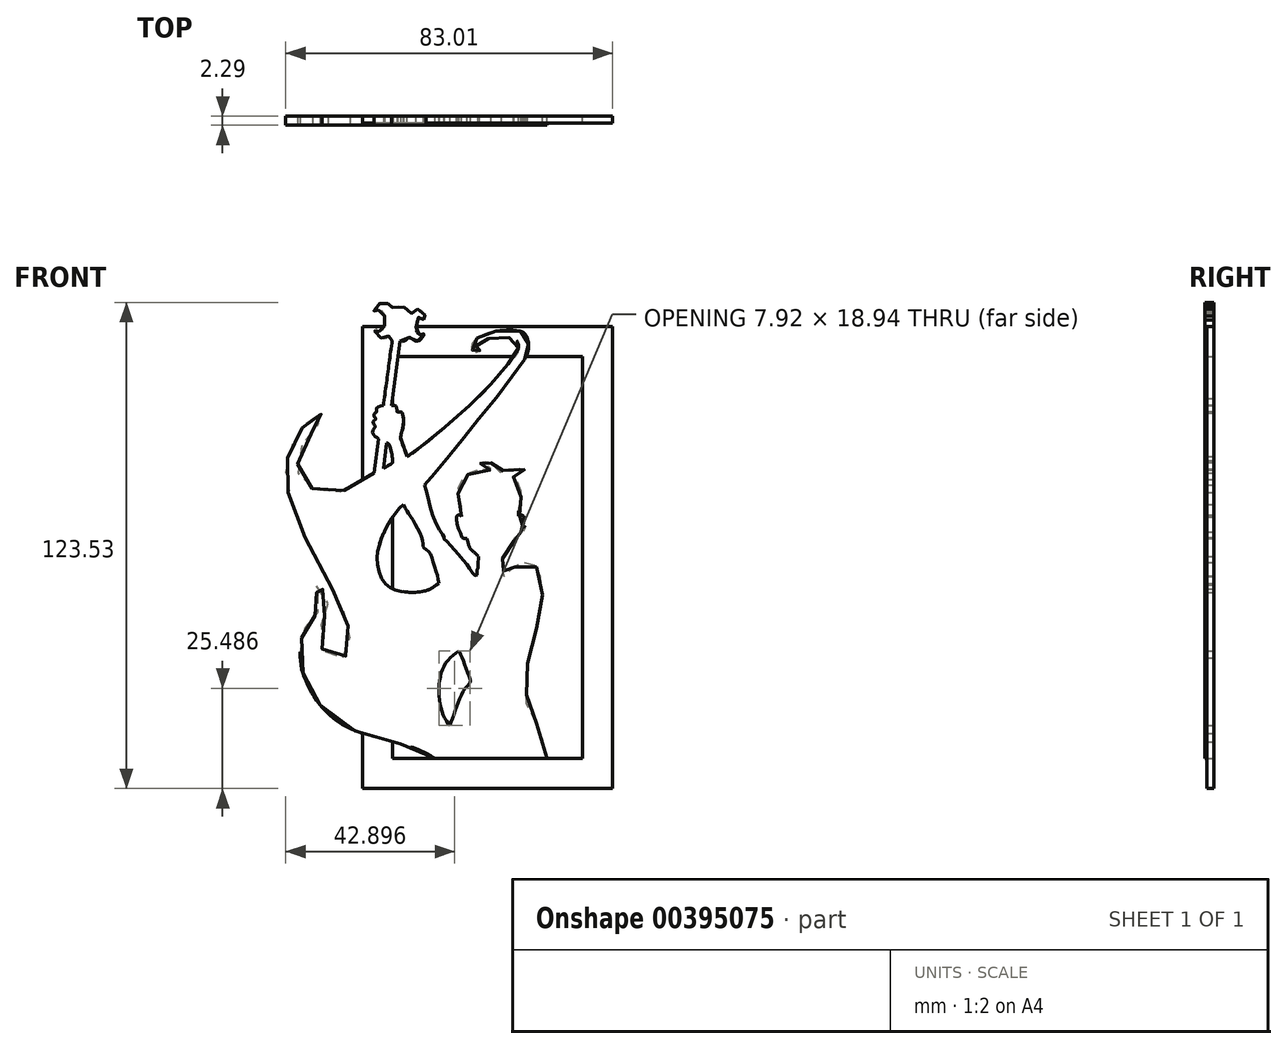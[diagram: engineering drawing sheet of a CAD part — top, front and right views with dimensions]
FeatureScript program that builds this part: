
annotation { "Feature Type Name" : "Feature", "Feature Type Description" : "" }
export const myFeature = defineFeature(function(context is Context, id is Id, definition is map)
    precondition{}
    {
        {
            var Q0;
            Q0=qCreatedBy(makeId("Front.planeOp"),FACE);
            var sketch = newSketch(context, id + "F0", { "sketchPlane" : qUnion([Q0])});
            skLineSegment(sketch, "E0.bottom", {"start": v(31.75, 58.67) * mm, "end": v(-31.75, 58.67) * mm});
            skLineSegment(sketch, "E0.top", {"start": v(31.75, -58.67) * mm, "end": v(-31.75, -58.67) * mm});
            skLineSegment(sketch, "E0.left", {"start": v(31.75, 58.67) * mm, "end": v(31.75, -58.67) * mm});
            skLineSegment(sketch, "E0.right", {"start": v(-31.75, 58.67) * mm, "end": v(-31.75, -58.67) * mm});
            skPoint(sketch, "E0.middle", {"position": v(0, 0) * mm});
            skLineSegment(sketch, "E1.0", {"start": v(-24.13, 51.05) * mm, "end": v(-24.13, -51.05) * mm});
            skLineSegment(sketch, "E1.1", {"start": v(24.13, 51.05) * mm, "end": v(-24.13, 51.05) * mm});
            skLineSegment(sketch, "E1.2", {"start": v(24.13, 51.05) * mm, "end": v(24.13, -51.05) * mm});
            skLineSegment(sketch, "E1.3", {"start": v(24.13, -51.05) * mm, "end": v(-24.13, -51.05) * mm});
            skSolve(sketch);
        }
        {
            var Q0;
            Q0=qSketchRegion(id+"F0",true);
            extrude(context, id + "F1", {"entities" : qUnion([Q0]), "depth" : 1.78 * mm});
        }
        {
            var Q0;
            Q0=qCreatedBy(makeId("Front.planeOp"),FACE);
            var sketch = newSketch(context, id + "F2", { "sketchPlane" : qUnion([Q0])});
            skLineSegment(sketch, "E2", {"start": v(-13.4, -51.05) * mm, "end": v(15.1, -51.05) * mm});
            skFitSpline(sketch, "E3", {"points": [v(15.1, -51.05) * mm, v(14.07, -46.67) * mm, v(12.43, -42.04) * mm, v(9.81, -36.93) * mm, v(9.63, -36.63) * mm, v(9.93, -34.8) * mm, v(10.11, -30.42) * mm, v(10, -28.05) * mm, v(10.78, -23.49) * mm, v(11.88, -19.96) * mm, v(13.1, -14.91) * mm, v(13.7, -11.8) * mm, v(13.89, -7.61) * mm, v(13.4, -4.75) * mm, v(12.55, -2.56) * mm, v(11.09, -1.47) * mm, v(9.26, -1.22) * mm, v(7.38, -2.07) * mm, v(5.8, -3.17) * mm, v(4.21, -4.81) * mm, v(4.14, -4.64) * mm, v(4.07, -4) * mm, v(3.98, -2.7) * mm, v(3.9, -1.79) * mm, v(3.64, -1.38) * mm, v(3.56, -0.75) * mm, v(3.58, -0.38) * mm, v(3.68, -0.29) * mm, v(4.73, 1.03) * mm, v(6.12, 2.95) * mm, v(6.51, 3.62) * mm, v(6.68, 4.16) * mm, v(6.81, 5.02) * mm, v(6.96, 5.1) * mm, v(7.28, 5.02) * mm, v(7.6, 5.21) * mm, v(8.02, 6) * mm, v(8.47, 6.55) * mm, v(8.64, 6.5) * mm, v(9, 6.57) * mm, v(9.37, 6.93) * mm, v(9.65, 7.2) * mm, v(9.74, 7.51) * mm, v(9.41, 7.86) * mm, v(8.96, 8.12) * mm, v(8.88, 8.22) * mm, v(9.1, 8.8) * mm, v(9.33, 9.94) * mm, v(9.1, 10.6) * mm, v(8.6, 10.87) * mm, v(8.06, 10.68) * mm, v(7.9, 10.61) * mm, v(7.82, 11.24) * mm, v(8.08, 13.09) * mm, v(8.49, 15.24) * mm, v(8.51, 17.21) * mm, v(7.93, 18.74) * mm, v(6.68, 20.42) * mm, v(6.57, 20.6) * mm, v(6.81, 21) * mm, v(7.84, 21.69) * mm, v(9.05, 21.99) * mm, v(9.28, 22.03) * mm, v(9.4, 22.3) * mm, v(9.18, 22.48) * mm, v(8.1, 22.57) * mm, v(6.34, 22.5) * mm, v(4.1, 22.18) * mm, v(3.11, 21.54) * mm, v(2.94, 21.52) * mm, v(2.75, 22.05) * mm, v(1.82, 23.2) * mm, v(0.72, 24.18) * mm, v(0.27, 24.27) * mm, v(-0.57, 24.36) * mm, v(-1.88, 24.33) * mm, v(-2, 24.14) * mm, v(-2.1, 24.03) * mm, v(-1.43, 23.93) * mm, v(-0.7, 23.84) * mm, v(0.06, 23.45) * mm, v(0.88, 22.55) * mm, v(0.94, 22.38) * mm, v(0.77, 22.3) * mm, v(-0.07, 22.38) * mm, v(-1.68, 22.5) * mm, v(-3.92, 21.84) * mm, v(-5.66, 20.66) * mm, v(-7, 19.1) * mm, v(-7.5, 17.62) * mm, v(-7.45, 15.99) * mm, v(-6.95, 14.07) * mm, v(-6.76, 12.57) * mm, v(-6.67, 10.48) * mm], "startDerivative": vector(-46.05, 210) * mm, "endDerivative": vector(5, -150.86) * mm});
            skFitSpline(sketch, "E4", {"points": [v(-6.67, 10.48) * mm, v(-6.98, 10.76) * mm, v(-7.56, 10.76) * mm, v(-7.86, 10.48) * mm, v(-7.86, 9.69) * mm, v(-7.75, 8.53) * mm, v(-7.36, 7.36) * mm, v(-6.67, 5.86) * mm, v(-6.4, 5.04) * mm, v(-6, 4.91) * mm, v(-5.5, 4.91) * mm, v(-5.23, 4.91) * mm], "startDerivative": vector(-3.53, 4.78) * mm, "endDerivative": vector(4.22, -0.04) * mm});
            skFitSpline(sketch, "E5", {"points": [v(-5.23, 4.91) * mm, v(-4.96, 3.81) * mm, v(-4.57, 2.56) * mm, v(-4.18, 2.09) * mm, v(-3, 1.01) * mm, v(-2.35, 0.35) * mm], "startDerivative": vector(1.27, -5.08) * mm, "endDerivative": vector(3, -3.27) * mm});
            skFitSpline(sketch, "E6", {"points": [v(-2.35, 0.35) * mm, v(-2.35, -2.34) * mm, v(-2.35, -2.62) * mm, v(-2.54, -2.68) * mm, v(-2.64, -2.87) * mm, v(-2.7, -3.57) * mm, v(-2.77, -4.6) * mm, v(-2.85, -4.6) * mm, v(-3.2, -4.52) * mm, v(-3.68, -4.07) * mm, v(-4.42, -3.05) * mm, v(-5.06, -1.92) * mm, v(-6.18, -0.65) * mm, v(-7.56, 1.04) * mm, v(-8.8, 2.46) * mm, v(-9.78, 3.55) * mm, v(-10.71, 4.44) * mm, v(-11.04, 4.73) * mm, v(-11.01, 4.82) * mm, v(-10.99, 5.13) * mm, v(-11.07, 5.59) * mm, v(-11.36, 5.9) * mm, v(-12.1, 6.94) * mm, v(-13.57, 9.83) * mm, v(-14.78, 13.68) * mm, v(-15.57, 17) * mm, v(-16.05, 18.49) * mm], "startDerivative": vector(-1.4, -53.24) * mm, "endDerivative": vector(-9.98, 28.07) * mm});
            skFitSpline(sketch, "E7", {"points": [v(-16.05, 18.49) * mm, v(-14.44, 20.22) * mm, v(-11.08, 24.27) * mm, v(-6.56, 29.7) * mm, v(-2.54, 34.9) * mm, v(3.63, 42.43) * mm, v(7.76, 48.1) * mm, v(10.1, 51.74) * mm, v(10.35, 54.81) * mm, v(9.05, 57.24) * mm, v(2.42, 57.56) * mm, v(-2.54, 55.86) * mm, v(-4.06, 53.76) * mm, v(-3.49, 52.3) * mm, v(-2.54, 52.3) * mm, v(-1.98, 52.6) * mm, v(-2.35, 52.97) * mm, v(-2.96, 53.2) * mm, v(-2.93, 53.79) * mm, v(-1.4, 55.05) * mm, v(2.82, 56) * mm, v(7.18, 55.28) * mm, v(7.75, 52.97) * mm, v(5.03, 48.99) * mm, v(-1.09, 42.07) * mm, v(-9.94, 33.99) * mm, v(-18.22, 27.16) * mm, v(-20.43, 25.76) * mm], "startDerivative": vector(51.48, 53.06) * mm, "endDerivative": vector(-61.57, -34.52) * mm});
            skFitSpline(sketch, "E8", {"points": [v(-21.38, 13.54) * mm, v(-23.4, 11.35) * mm, v(-25.9, 7.27) * mm, v(-27.77, 2.2) * mm, v(-27.9, -1.84) * mm, v(-26.2, -6.4) * mm, v(-23.52, -8.1) * mm, v(-19.48, -8.8) * mm, v(-14.86, -8.1) * mm, v(-13.2, -7.06) * mm, v(-12.32, -6.57) * mm], "startDerivative": vector(-21.98, -21.6) * mm, "endDerivative": vector(16.25, 7.7) * mm});
            skFitSpline(sketch, "E9", {"points": [v(-12.32, -6.57) * mm, v(-12.92, -3.86) * mm, v(-14.01, -0.42) * mm, v(-14.9, 1.56) * mm, v(-16.05, 2.41) * mm, v(-16.4, 2.94) * mm, v(-16.44, 4.15) * mm, v(-17.5, 6.94) * mm, v(-19.27, 10.14) * mm, v(-20.37, 11.68) * mm, v(-21.38, 13.54) * mm], "startDerivative": vector(-4.4, 22.74) * mm, "endDerivative": vector(-9.9, 19.78) * mm});
            skFitSpline(sketch, "E10", {"points": [v(-20.43, 25.76) * mm, v(-22.05, 30.3) * mm, v(-22.05, 30.93) * mm, v(-21.38, 34.16) * mm, v(-21.62, 36.65) * mm, v(-21.83, 36.92) * mm, v(-22.26, 36.96) * mm, v(-22.9, 36.98) * mm, v(-23.02, 37.14) * mm, v(-23.02, 37.92) * mm, v(-23.43, 38.6) * mm, v(-23.82, 38.67) * mm, v(-24.35, 38.64) * mm], "startDerivative": vector(-11.78, 31.34) * mm, "endDerivative": vector(-9.1, -0.56) * mm});
            skFitSpline(sketch, "E11", {"points": [v(-24.35, 38.64) * mm, v(-22.2, 55) * mm], "startDerivative": vector(2.14, 16.36) * mm, "endDerivative": vector(2.14, 16.36) * mm});
            skFitSpline(sketch, "E12", {"points": [v(-26.49, 38.64) * mm, v(-24.21, 55.2) * mm], "startDerivative": vector(2.38, 16.57) * mm, "endDerivative": vector(2.38, 16.57) * mm});
            skFitSpline(sketch, "E13", {"points": [v(-27.68, 30.19) * mm, v(-28.84, 21.57) * mm], "startDerivative": vector(-1.15, -8.61) * mm, "endDerivative": vector(-1.15, -8.61) * mm});
            skFitSpline(sketch, "E14", {"points": [v(-25.71, 29.13) * mm, v(-26.43, 22.68) * mm], "startDerivative": vector(-0.72, -6.45) * mm, "endDerivative": vector(-0.72, -6.45) * mm});
            skFitSpline(sketch, "E15", {"points": [v(-22.2, 55) * mm, v(-20.81, 55.2) * mm, v(-19.8, 56) * mm, v(-18.75, 55.2) * mm, v(-17.3, 55.2) * mm, v(-16.28, 56.5) * mm, v(-16.2, 56.74) * mm, v(-16.26, 56.92) * mm, v(-16.75, 56.72) * mm, v(-17.25, 56.72) * mm, v(-17.9, 57.3) * mm, v(-18.22, 58.17) * mm, v(-18.08, 59.68) * mm, v(-17.68, 60.96) * mm, v(-17.03, 61.38) * mm, v(-16.52, 60.93) * mm, v(-16.2, 60.47) * mm, v(-15.78, 60.51) * mm, v(-15.66, 60.97) * mm, v(-16.36, 62.31) * mm, v(-17.45, 63.13) * mm, v(-18.36, 62.87) * mm, v(-19.08, 62.04) * mm, v(-19.24, 62.09) * mm, v(-20, 62.93) * mm, v(-21.57, 63.82) * mm, v(-23.57, 63.77) * mm, v(-24.35, 63.4) * mm, v(-24.35, 63.56) * mm, v(-25.19, 64.43) * mm, v(-25.97, 64.83) * mm, v(-27.22, 64.66) * mm, v(-28.48, 63.6) * mm, v(-28.88, 62.83) * mm, v(-28.7, 62.46) * mm, v(-28.42, 62.43) * mm, v(-27.88, 62.73) * mm, v(-27.43, 62.97) * mm, v(-26.36, 62.07) * mm, v(-26.07, 60.63) * mm, v(-26.15, 59.08) * mm, v(-26.68, 57.98) * mm, v(-27.32, 57.5) * mm, v(-27.93, 57.64) * mm, v(-28.22, 58.04) * mm, v(-28.66, 57.78) * mm, v(-28.3, 56.98) * mm, v(-27.36, 56) * mm, v(-25.95, 55.8) * mm, v(-25.22, 56.23) * mm, v(-25.02, 56.23) * mm, v(-24.69, 55.76) * mm, v(-24.35, 55.38) * mm, v(-24.21, 55.2) * mm], "startDerivative": vector(61, -3.49) * mm, "endDerivative": vector(21.54, -13.38) * mm});
            skFitSpline(sketch, "E16", {"points": [v(-26.43, 22.68) * mm, v(-25, 23.53) * mm, v(-24.35, 23.94) * mm, v(-24.06, 24.26) * mm, v(-24.08, 24.4) * mm, v(-24.21, 25.67) * mm, v(-24.63, 27.78) * mm, v(-25.16, 28.98) * mm, v(-25.71, 29.13) * mm], "startDerivative": vector(10.83, 5.27) * mm, "endDerivative": vector(-6.22, 0.36) * mm});
            skFitSpline(sketch, "E17", {"points": [v(-28.84, 21.57) * mm, v(-34.02, 18.49) * mm, v(-38.02, 16.6) * mm, v(-43.02, 16.99) * mm, v(-46.92, 19.2) * mm, v(-48.26, 23.2) * mm, v(-46.77, 29.13) * mm, v(-43.16, 33.88) * mm, v(-42.3, 34.74) * mm, v(-42.06, 35.95) * mm, v(-42.4, 36.52) * mm, v(-43.84, 36.19) * mm, v(-46.53, 33.64) * mm, v(-48.9, 30.32) * mm, v(-50.91, 24.83) * mm, v(-51.15, 19.54) * mm, v(-49.47, 12.88) * mm, v(-43.93, 0.35) * mm, v(-37.37, -11.93) * mm, v(-35.51, -17.27) * mm, v(-34.98, -22.19) * mm, v(-36.4, -25.25) * mm, v(-40.08, -25.25) * mm, v(-42.2, -22.73) * mm, v(-42.12, -16.88) * mm, v(-40.83, -13.34) * mm, v(-40.7, -10) * mm, v(-43.23, -7.13) * mm, v(-44.38, -7.42) * mm, v(-44.33, -8.1) * mm, v(-42.94, -9.2) * mm, v(-42.27, -11.9) * mm, v(-44.14, -15.02) * mm, v(-46.26, -17.52) * mm, v(-47.32, -20.55) * mm, v(-47.56, -26.18) * mm, v(-46.07, -31.57) * mm, v(-42.8, -37.1) * mm, v(-36.68, -42.54) * mm, v(-26.97, -46.05) * mm, v(-18.22, -48.5) * mm, v(-13.4, -51.05) * mm], "startDerivative": vector(-190.43, -112.05) * mm, "endDerivative": vector(158.52, -121.25) * mm});
            skFitSpline(sketch, "E18", {"points": [v(-7.22, -23.71) * mm, v(-5.68, -27.43) * mm, v(-4.42, -31.1) * mm, v(-4.48, -31.78) * mm, v(-5.96, -33.61) * mm, v(-8.02, -38.3) * mm, v(-9.57, -42.65) * mm], "startDerivative": vector(8.08, -18.75) * mm, "endDerivative": vector(-7.48, -20.99) * mm});
            skFitSpline(sketch, "E19", {"points": [v(-7.22, -23.71) * mm, v(-10.43, -26.46) * mm, v(-12.03, -30.47) * mm, v(-12.31, -35.16) * mm, v(-11.23, -40.02) * mm, v(-9.57, -42.65) * mm], "startDerivative": vector(-17.85, -12.27) * mm, "endDerivative": vector(10.47, -13.68) * mm});
            skFitSpline(sketch, "E20", {"points": [v(-26.49, 38.64) * mm, v(-27.78, 38.33) * mm, v(-28.2, 37.99) * mm, v(-28.16, 37.44) * mm, v(-28.2, 37.04) * mm, v(-28.35, 36.82) * mm, v(-28.71, 36.65) * mm, v(-28.9, 36) * mm, v(-28.43, 35.44) * mm, v(-28.52, 35.08) * mm, v(-29.1, 34.7) * mm, v(-28.9, 33.93) * mm, v(-28.54, 33.35) * mm, v(-28.71, 32.96) * mm, v(-29.16, 32.37) * mm, v(-29.12, 31.44) * mm, v(-28.28, 30.65) * mm, v(-27.68, 30.19) * mm], "startDerivative": vector(-16.9, -3.26) * mm, "endDerivative": vector(8.6, -6.94) * mm});
            skSolve(sketch);
        }
        {
            var Q0;
            Q0 = qSketchRegion(id + "F2", true);
            extrude(context, id + "F3", {"entities" : qUnion([Q0]), "operationType" : NewBodyOperationType.ADD, "depth" : 2.3 * mm});
        }
        {
            var Q0;
            Q0=makeQuery(id+"F3.opExtrude","CAP_FACE",FACE,{"disambiguationData":[OSD([sQuery(id+"F2.wireOp",EDGE,"E2"),sQuery(id+"F2.wireOp",EDGE,"E3"),sQuery(id+"F2.wireOp",EDGE,"E4"),sQuery(id+"F2.wireOp",EDGE,"E5"),sQuery(id+"F2.wireOp",EDGE,"E6"),sQuery(id+"F2.wireOp",EDGE,"E7"),sQuery(id+"F2.wireOp",EDGE,"E8"),sQuery(id+"F2.wireOp",EDGE,"E9"),sQuery(id+"F2.wireOp",EDGE,"E10"),sQuery(id+"F2.wireOp",EDGE,"E11"),sQuery(id+"F2.wireOp",EDGE,"E12"),sQuery(id+"F2.wireOp",EDGE,"E13"),sQuery(id+"F2.wireOp",EDGE,"E14"),sQuery(id+"F2.wireOp",EDGE,"E15"),sQuery(id+"F2.wireOp",EDGE,"E16"),sQuery(id+"F2.wireOp",EDGE,"E17"),sQuery(id+"F2.wireOp",EDGE,"E18"),sQuery(id+"F2.wireOp",EDGE,"E19"),sQuery(id+"F2.wireOp",EDGE,"E20")])],"isStart":false});
            var sketch = newSketch(context, id + "F4", { "sketchPlane" : qUnion([Q0])});
            skFitSpline(sketch, "E21", {"points": [v(-7.2, 9.05) * mm, v(-6.76, 8.3) * mm, v(-6.3, 7.67) * mm], "startDerivative": vector(0.82, -1.5) * mm, "endDerivative": vector(1, -1.24) * mm});
            skFitSpline(sketch, "E22", {"points": [v(-5.54, 6.57) * mm, v(-5.39, 5.64) * mm, v(-5.31, 5.12) * mm], "startDerivative": vector(0.3, -1.75) * mm, "endDerivative": vector(0.16, -1.12) * mm});
            skFitSpline(sketch, "E23", {"points": [v(-6.57, 10.34) * mm, v(-6.14, 9.6) * mm, v(-5.56, 8.59) * mm, v(-5.54, 8.75) * mm, v(-5.54, 11) * mm, v(-5.64, 12.95) * mm, v(-4.93, 15.58) * mm, v(-4.48, 16.16) * mm, v(-4.34, 16.17) * mm, v(-4.18, 15.4) * mm, v(-3.71, 13.67) * mm, v(-2.7, 12.31) * mm, v(-2.26, 11.98) * mm, v(-2.12, 12.33) * mm, v(-1.94, 13.7) * mm, v(-0.41, 16.17) * mm, v(0.35, 16.83) * mm, v(0.53, 16.83) * mm, v(1.18, 16.38) * mm, v(2.03, 15.52) * mm, v(3.01, 13.36) * mm, v(3.4, 12.3) * mm, v(3.6, 12.14) * mm, v(3.86, 12.1) * mm, v(4.72, 13.44) * mm, v(5.55, 15.16) * mm, v(5.94, 15.36) * mm, v(6.17, 15.06) * mm, v(6.47, 13.64) * mm, v(6.76, 10.98) * mm, v(6.74, 8.65) * mm, v(6.84, 8.29) * mm, v(7.05, 8.2) * mm, v(7.24, 9.05) * mm, v(7.84, 10.5) * mm], "startDerivative": vector(14.17, -22.21) * mm, "endDerivative": vector(20.52, 38.76) * mm});
            skFitSpline(sketch, "E24", {"points": [v(7.05, 7.94) * mm, v(7.02, 7.04) * mm, v(6.85, 5.88) * mm, v(6.9, 5.35) * mm], "startDerivative": vector(0.04, -2.48) * mm, "endDerivative": vector(0.33, -1.79) * mm});
            skFitSpline(sketch, "E25", {"points": [v(8.87, 8.02) * mm, v(8.45, 8) * mm, v(8.5, 7.5) * mm, v(8.98, 7.24) * mm, v(9.32, 7.07) * mm], "startDerivative": vector(-2.15, 0.38) * mm, "endDerivative": vector(1.37, -0.8) * mm});
            skFitSpline(sketch, "E26", {"points": [v(8.5, 7.32) * mm, v(8.48, 7.02) * mm, v(8.52, 6.74) * mm], "startDerivative": vector(-0.1, -0.6) * mm, "endDerivative": vector(0.13, -0.57) * mm});
            skFitSpline(sketch, "E27", {"points": [v(-6.67, 15.66) * mm, v(-6.32, 17.88) * mm, v(-4.47, 19.57) * mm, v(-2.44, 19.94) * mm], "startDerivative": vector(0.06, 6.93) * mm, "endDerivative": vector(6.4, 0.37) * mm});
            skFitSpline(sketch, "E28", {"points": [v(-4.28, 19.97) * mm, v(-3.31, 20.91) * mm, v(-0.94, 21.48) * mm, v(0.81, 21.38) * mm, v(1.35, 20.88) * mm], "startDerivative": vector(3.31, 4.38) * mm, "endDerivative": vector(2.42, -3.33) * mm});
            skFitSpline(sketch, "E29", {"points": [v(2.93, 21.03) * mm, v(3.66, 21.22) * mm, v(4.12, 21.74) * mm], "startDerivative": vector(1.56, 0.19) * mm, "endDerivative": vector(0.8, 1.23) * mm});
            skFitSpline(sketch, "E30", {"points": [v(-2.88, 9.75) * mm, v(-2.83, 9.25) * mm, v(-2.35, 8.83) * mm, v(-2.03, 8.87) * mm, v(-1.73, 9.4) * mm, v(-1.69, 9.63) * mm], "startDerivative": vector(-0.2, -2.4) * mm, "endDerivative": vector(0.08, 1.38) * mm});
            skFitSpline(sketch, "E31", {"points": [v(-3.76, 8.94) * mm, v(-4.1, 9.58) * mm, v(-3.6, 10.2) * mm, v(-2.73, 10) * mm, v(-1.6, 9.85) * mm, v(-0.42, 9.54) * mm], "startDerivative": vector(-2.96, 3.38) * mm, "endDerivative": vector(5.18, -1.68) * mm});
            skFitSpline(sketch, "E32", {"points": [v(0.04, 9.9) * mm, v(-1.06, 10.18) * mm, v(-2.35, 10.8) * mm, v(-3.67, 11.55) * mm], "startDerivative": vector(-3.54, 0.76) * mm, "endDerivative": vector(-3.71, 2.15) * mm});
            skFitSpline(sketch, "E33", {"points": [v(2.7, 9.67) * mm, v(3.48, 10.08) * mm, v(5.05, 10.2) * mm, v(5.7, 10) * mm, v(5.65, 9.68) * mm, v(5.07, 8.93) * mm], "startDerivative": vector(3.3, 2.27) * mm, "endDerivative": vector(-3.22, -3.72) * mm});
            skFitSpline(sketch, "E34", {"points": [v(3.32, 9.8) * mm, v(3.53, 9.23) * mm, v(3.88, 8.97) * mm, v(4.28, 9.05) * mm, v(4.48, 9.43) * mm, v(4.48, 10.04) * mm], "startDerivative": vector(0.75, -2.77) * mm, "endDerivative": vector(-0.21, 2.84) * mm});
            skFitSpline(sketch, "E35", {"points": [v(2.53, 10.14) * mm, v(3.44, 10.7) * mm, v(4.44, 11.11) * mm, v(5.7, 11.5) * mm], "startDerivative": vector(2.8, 1.82) * mm, "endDerivative": vector(3.61, 1.08) * mm});
            skFitSpline(sketch, "E36", {"points": [v(0.68, 5.35) * mm, v(0.51, 5.26) * mm, v(0.52, 5.03) * mm, v(0.8, 4.91) * mm, v(0.87, 5.19) * mm, v(0.68, 5.35) * mm]});
            skFitSpline(sketch, "E37", {"points": [v(1.76, 5.07) * mm, v(2.03, 5.35) * mm, v(2.3, 5.35) * mm, v(2.46, 5.2) * mm, v(2.28, 4.82) * mm, v(2.03, 4.7) * mm, v(1.8, 4.82) * mm, v(1.76, 5.07) * mm]});
            skFitSpline(sketch, "E38", {"points": [v(-0.32, 2.15) * mm, v(0.53, 3.03) * mm, v(1.77, 3.52) * mm, v(2.66, 3.36) * mm, v(3.06, 2.73) * mm], "startDerivative": vector(2.82, 3.52) * mm, "endDerivative": vector(1.45, -3.44) * mm});
            skFitSpline(sketch, "E39", {"points": [v(-0.05, 2.2) * mm, v(1.41, 2.6) * mm, v(2.38, 2.74) * mm, v(2.88, 2.74) * mm], "startDerivative": vector(3.6, 1.11) * mm, "endDerivative": vector(1.93, -0.06) * mm});
            skFitSpline(sketch, "E40", {"points": [v(2.5, 2.62) * mm, v(2.42, 2.12) * mm, v(1.81, 1.71) * mm, v(0.9, 1.69) * mm], "startDerivative": vector(0.03, -1.85) * mm, "endDerivative": vector(-2.49, 0.2) * mm});
            skFitSpline(sketch, "E41", {"points": [v(-2.14, 0.22) * mm, v(-0.9, -0.86) * mm, v(0.6, -1.34) * mm, v(2.1, -1.1) * mm, v(3.3, -0.49) * mm], "startDerivative": vector(4.54, -4.57) * mm, "endDerivative": vector(4.85, 2.9) * mm});
            skFitSpline(sketch, "E42", {"points": [v(0.13, -5.71) * mm, v(0.18, -6.81) * mm], "startDerivative": vector(0.06, -1.1) * mm, "endDerivative": vector(0.06, -1.1) * mm});
            skFitSpline(sketch, "E43", {"points": [v(1.4, -5.77) * mm, v(1.39, -6.94) * mm], "startDerivative": vector(-0.02, -1.17) * mm, "endDerivative": vector(-0.02, -1.17) * mm});
            skFitSpline(sketch, "E44", {"points": [v(-0.05, -9.73) * mm, v(1.33, -9.82) * mm, v(2.23, -9.75) * mm, v(2.28, -9.53) * mm, v(2.28, -7.65) * mm, v(2.34, -7.39) * mm, v(2.7, -6.85) * mm, v(2.75, -4.84) * mm, v(2.17, -3.78) * mm, v(1.05, -3.28) * mm, v(-0.32, -3.56) * mm, v(-1.05, -4.34) * mm, v(-1.27, -5.83) * mm, v(-0.95, -7.03) * mm, v(-0.62, -7.39) * mm, v(-0.32, -7.7) * mm, v(-0.05, -7.9) * mm, v(-0.05, -8.19) * mm, v(-0.05, -9.49) * mm, v(-0.05, -9.73) * mm]});
            skFitSpline(sketch, "E45", {"points": [v(-2.69, -4.87) * mm, v(-2.07, -5.5) * mm, v(-1.45, -6.05) * mm], "startDerivative": vector(1.21, -1.25) * mm, "endDerivative": vector(1.26, -1.1) * mm});
            skFitSpline(sketch, "E46", {"points": [v(3.77, -3.02) * mm, v(3.41, -3.52) * mm, v(2.62, -3.99) * mm], "startDerivative": vector(-0.64, -1.2) * mm, "endDerivative": vector(-1.63, -0.77) * mm});
            skFitSpline(sketch, "E47", {"points": [v(4.1, -5.05) * mm, v(3.52, -5.71) * mm, v(3, -6.27) * mm], "startDerivative": vector(-1.12, -1.32) * mm, "endDerivative": vector(-1.1, -1.11) * mm});
            skFitSpline(sketch, "E48", {"points": [v(-1.06, -3.8) * mm, v(-1.75, -3.45) * mm, v(-2.32, -2.84) * mm], "startDerivative": vector(-1.47, 0.6) * mm, "endDerivative": vector(-1.05, 1.34) * mm});
            skSolve(sketch);
        }
        {
            var Q0;
            Q0 = qSketchRegion(id + "F4", true);
            var Q1;
            Q1=sQuery(id+"F4.wireOp",EDGE,"E27");
            var Q2;
            Q2=sQuery(id+"F4.wireOp",EDGE,"E28");
            var Q3;
            Q3=sQuery(id+"F4.wireOp",EDGE,"E29");
            var Q4;
            Q4=sQuery(id+"F4.wireOp",EDGE,"E23");
            var Q5;
            Q5=sQuery(id+"F4.wireOp",EDGE,"E21");
            var Q6;
            Q6=sQuery(id+"F4.wireOp",EDGE,"E22");
            var Q7;
            Q7=sQuery(id+"F4.wireOp",EDGE,"E30");
            var Q8;
            Q8=sQuery(id+"F4.wireOp",EDGE,"E32");
            var Q9;
            Q9=sQuery(id+"F4.wireOp",EDGE,"E31");
            var Q10;
            Q10=sQuery(id+"F4.wireOp",EDGE,"E35");
            var Q11;
            Q11=sQuery(id+"F4.wireOp",EDGE,"E33");
            var Q12;
            Q12=sQuery(id+"F4.wireOp",EDGE,"E34");
            var Q13;
            Q13=sQuery(id+"F4.wireOp",EDGE,"E37");
            var Q14;
            Q14=sQuery(id+"F4.wireOp",EDGE,"E36");
            var Q15;
            Q15=sQuery(id+"F4.wireOp",EDGE,"E38");
            var Q16;
            Q16=sQuery(id+"F4.wireOp",EDGE,"E39");
            var Q17;
            Q17=sQuery(id+"F4.wireOp",EDGE,"E25");
            var Q18;
            Q18=sQuery(id+"F4.wireOp",EDGE,"E26");
            var Q19;
            Q19=sQuery(id+"F4.wireOp",EDGE,"E24");
            var Q20;
            Q20=sQuery(id+"F4.wireOp",EDGE,"E40");
            var Q21;
            Q21=sQuery(id+"F4.wireOp",EDGE,"E41");
            var Q22;
            Q22=sQuery(id+"F4.wireOp",EDGE,"61576300-be42-430f-bdc8-9e316a19b665");
            var Q23;
            Q23=sQuery(id+"F4.wireOp",EDGE,"E45");
            var Q24;
            Q24=sQuery(id+"F4.wireOp",EDGE,"E44");
            var Q25;
            Q25=sQuery(id+"F4.wireOp",EDGE,"E42");
            var Q26;
            Q26=sQuery(id+"F4.wireOp",EDGE,"E43");
            var Q27;
            Q27=sQuery(id+"F4.wireOp",EDGE,"E47");
            var Q28;
            Q28=sQuery(id+"F4.wireOp",EDGE,"E46");
            var Q29;
            Q29=sQuery(id+"F4.wireOp",EDGE,"E48");
            extrude(context, id + "F5", {"entities" : qUnion([Q0]), "bodyType" : ToolBodyType.SURFACE, "surfaceEntities" : qUnion([Q1, Q2, Q3, Q4, Q5, Q6, Q7, Q8, Q9, Q10, Q11, Q12, Q13, Q14, Q15, Q16, Q17, Q18, Q19, Q20, Q21, Q22, Q23, Q24, Q25, Q26, Q27, Q28, Q29]), "depth" : 0.25 * mm});
        }
        {
            var Q0;
            Q0=makeQuery(id+"F3.opExtrude","CAP_FACE",FACE,{"disambiguationData":[OSD([sQuery(id+"F2.wireOp",EDGE,"E2"),sQuery(id+"F2.wireOp",EDGE,"E3"),sQuery(id+"F2.wireOp",EDGE,"E4"),sQuery(id+"F2.wireOp",EDGE,"E5"),sQuery(id+"F2.wireOp",EDGE,"E6"),sQuery(id+"F2.wireOp",EDGE,"E7"),sQuery(id+"F2.wireOp",EDGE,"E8"),sQuery(id+"F2.wireOp",EDGE,"E9"),sQuery(id+"F2.wireOp",EDGE,"E10"),sQuery(id+"F2.wireOp",EDGE,"E11"),sQuery(id+"F2.wireOp",EDGE,"E12"),sQuery(id+"F2.wireOp",EDGE,"E13"),sQuery(id+"F2.wireOp",EDGE,"E14"),sQuery(id+"F2.wireOp",EDGE,"E15"),sQuery(id+"F2.wireOp",EDGE,"E16"),sQuery(id+"F2.wireOp",EDGE,"E17"),sQuery(id+"F2.wireOp",EDGE,"E18"),sQuery(id+"F2.wireOp",EDGE,"E19"),sQuery(id+"F2.wireOp",EDGE,"E20")])],"isStart":false});
            var sketch = newSketch(context, id + "F6", { "sketchPlane" : qUnion([Q0])});
            skFitSpline(sketch, "E49", {"points": [v(-12.01, -7.1) * mm, v(-10.75, -10.99) * mm, v(-9.16, -17.21) * mm, v(-7.35, -23.32) * mm], "startDerivative": vector(4.46, -12.7) * mm, "endDerivative": vector(5.24, -16.8) * mm});
            skFitSpline(sketch, "E50", {"points": [v(-8.7, -17.72) * mm, v(-7.22, -14.37) * mm, v(-4.67, -11.44) * mm, v(-2.74, -10.65) * mm, v(-0.52, -11.3) * mm, v(1.55, -13.47) * mm, v(1.96, -13.9) * mm, v(2.04, -13.82) * mm, v(3.18, -12.25) * mm, v(5.05, -10.5) * mm, v(7.2, -10.16) * mm, v(8.99, -11.13) * mm, v(9.74, -12.19) * mm, v(10.3, -12.8) * mm], "startDerivative": vector(11.18, 31) * mm, "endDerivative": vector(11.41, -10.59) * mm});
            skFitSpline(sketch, "E51", {"points": [v(9.97, -9.38) * mm, v(10.46, -12.05) * mm, v(10.52, -15.16) * mm, v(9.64, -18.9) * mm, v(8.46, -21.52) * mm, v(7.3, -25.6) * mm, v(7, -26.97) * mm, v(6.69, -27.83) * mm, v(6.3, -28.56) * mm, v(6.65, -31.7) * mm, v(7.32, -33.1) * mm, v(7.91, -34.12) * mm, v(8.67, -35.3) * mm, v(9.34, -36.31) * mm], "startDerivative": vector(6.3, -29.8) * mm, "endDerivative": vector(11.15, -15.72) * mm});
            skFitSpline(sketch, "E52", {"points": [v(7.9, -33.31) * mm, v(8, -31.78) * mm, v(7.89, -30.44) * mm, v(7.45, -29.9) * mm, v(7.61, -29.57) * mm, v(8.48, -29.65) * mm, v(9.6, -28.75) * mm], "startDerivative": vector(0.46, 7.25) * mm, "endDerivative": vector(5.32, 6.38) * mm});
            skFitSpline(sketch, "E53", {"points": [v(-7.96, -42.84) * mm, v(-6.79, -39.44) * mm, v(-4.45, -34.93) * mm, v(-3.06, -32.65) * mm, v(-3.11, -30.1) * mm, v(-5.23, -25.2) * mm, v(-6.79, -20.69) * mm, v(-7.45, -18.52) * mm, v(-7.51, -17.3) * mm], "startDerivative": vector(7.42, 24.51) * mm, "endDerivative": vector(0.44, 15.35) * mm});
            skFitSpline(sketch, "E54", {"points": [v(-0.33, -17.63) * mm, v(2.4, -18.96) * mm, v(3.45, -19.57) * mm, v(4.57, -20.63) * mm, v(4.57, -21.13) * mm], "startDerivative": vector(8.53, -4.14) * mm, "endDerivative": vector(-0.87, -3.16) * mm});
            skFitSpline(sketch, "E55", {"points": [v(-0.72, -21.24) * mm, v(0.73, -19.85) * mm, v(2.21, -19.16) * mm], "startDerivative": vector(2.66, 2.96) * mm, "endDerivative": vector(3.21, 1.18) * mm});
            skFitSpline(sketch, "E56", {"points": [v(5.16, -17.09) * mm, v(4.38, -17.9) * mm, v(3.15, -18.96) * mm, v(2.94, -18.96) * mm], "startDerivative": vector(-1.76, -1.88) * mm, "endDerivative": vector(-1.06, 0.35) * mm});
            skFitSpline(sketch, "E57", {"points": [v(-11.4, -50.53) * mm, v(-10.15, -46.75) * mm, v(-8.97, -43.48) * mm], "startDerivative": vector(2.43, 7.45) * mm, "endDerivative": vector(2.45, 6.63) * mm});
            skFitSpline(sketch, "E58", {"points": [v(-8.97, -43.48) * mm, v(-8.97, -47.1) * mm, v(-8.61, -48.76) * mm, v(-8.38, -49.9) * mm, v(-8.28, -50.83) * mm], "startDerivative": vector(-0.46, -10.95) * mm, "endDerivative": vector(0.41, -4.96) * mm});
            skFitSpline(sketch, "E59", {"points": [v(9.64, -13.65) * mm, v(8.47, -18.9) * mm, v(6.08, -25.06) * mm, v(5.3, -30.12) * mm, v(7.32, -35.35) * mm, v(10.75, -40.92) * mm, v(12.98, -46.49) * mm, v(13.43, -49.6) * mm], "startDerivative": vector(-6.03, -36.17) * mm, "endDerivative": vector(2.13, -26.61) * mm});
            skSolve(sketch);
        }
        {
            var Q0;
            Q0 = qSketchRegion(id + "F6", true);
            var Q1;
            Q1=sQuery(id+"F6.wireOp",EDGE,"E56");
            var Q2;
            Q2=sQuery(id+"F6.wireOp",EDGE,"E54");
            var Q3;
            Q3=sQuery(id+"F6.wireOp",EDGE,"E55");
            var Q4;
            Q4=sQuery(id+"F6.wireOp",EDGE,"E58");
            var Q5;
            Q5=sQuery(id+"F6.wireOp",EDGE,"E57");
            var Q6;
            Q6=sQuery(id+"F6.wireOp",EDGE,"E53");
            var Q7;
            Q7=sQuery(id+"F6.wireOp",EDGE,"E49");
            var Q8;
            Q8=sQuery(id+"F6.wireOp",EDGE,"E50");
            var Q9;
            Q9=sQuery(id+"F6.wireOp",EDGE,"E59");
            var Q10;
            Q10=sQuery(id+"F6.wireOp",EDGE,"E51");
            var Q11;
            Q11=sQuery(id+"F6.wireOp",EDGE,"E52");
            extrude(context, id + "F7", {"entities" : qUnion([Q0]), "bodyType" : ToolBodyType.SURFACE, "surfaceEntities" : qUnion([Q1, Q2, Q3, Q4, Q5, Q6, Q7, Q8, Q9, Q10, Q11]), "depth" : 0.25 * mm});
        }
        {
            var Q0;
            Q0=makeQuery(id+"F3.opExtrude","CAP_FACE",FACE,{"disambiguationData":[OSD([sQuery(id+"F2.wireOp",EDGE,"E2"),sQuery(id+"F2.wireOp",EDGE,"E3"),sQuery(id+"F2.wireOp",EDGE,"E4"),sQuery(id+"F2.wireOp",EDGE,"E5"),sQuery(id+"F2.wireOp",EDGE,"E6"),sQuery(id+"F2.wireOp",EDGE,"E7"),sQuery(id+"F2.wireOp",EDGE,"E8"),sQuery(id+"F2.wireOp",EDGE,"E9"),sQuery(id+"F2.wireOp",EDGE,"E10"),sQuery(id+"F2.wireOp",EDGE,"E11"),sQuery(id+"F2.wireOp",EDGE,"E12"),sQuery(id+"F2.wireOp",EDGE,"E13"),sQuery(id+"F2.wireOp",EDGE,"E14"),sQuery(id+"F2.wireOp",EDGE,"E15"),sQuery(id+"F2.wireOp",EDGE,"E16"),sQuery(id+"F2.wireOp",EDGE,"E17"),sQuery(id+"F2.wireOp",EDGE,"E18"),sQuery(id+"F2.wireOp",EDGE,"E19"),sQuery(id+"F2.wireOp",EDGE,"E20")])],"isStart":false});
            var sketch = newSketch(context, id + "F8", { "sketchPlane" : qUnion([Q0])});
            skFitSpline(sketch, "E60", {"points": [v(-24.06, 55.15) * mm, v(-23.13, 54.88) * mm, v(-23, 54.9) * mm, v(-22.62, 55) * mm, v(-22.37, 55) * mm], "startDerivative": vector(2.92, -0.9) * mm, "endDerivative": vector(1.14, -0.12) * mm});
            skFitSpline(sketch, "E61", {"points": [v(-26.24, 38.64) * mm, v(-25.46, 38.51) * mm, v(-24.63, 38.64) * mm], "startDerivative": vector(1.57, -0.37) * mm, "endDerivative": vector(1.66, 0.37) * mm});
            skFitSpline(sketch, "E62", {"points": [v(-28.24, 32.58) * mm, v(-27.77, 32.98) * mm, v(-26.35, 33.07) * mm, v(-25.5, 33) * mm], "startDerivative": vector(1.3, 1.71) * mm, "endDerivative": vector(2.34, -0.24) * mm});
            skFitSpline(sketch, "E63", {"points": [v(-27.77, 35.2) * mm, v(-26.11, 35.2) * mm, v(-24.92, 35.3) * mm], "startDerivative": vector(3.2, -0.06) * mm, "endDerivative": vector(2.5, 0.25) * mm});
            skFitSpline(sketch, "E64", {"points": [v(-27.68, 37.12) * mm, v(-26.09, 37.05) * mm, v(-24.85, 36.88) * mm, v(-24.35, 36.81) * mm], "startDerivative": vector(3.92, -0.08) * mm, "endDerivative": vector(1.93, -0.26) * mm});
            skFitSpline(sketch, "E65", {"points": [v(-22.44, 36.46) * mm, v(-22.2, 35.48) * mm, v(-22.2, 33.65) * mm, v(-22.65, 32.06) * mm], "startDerivative": vector(0.96, -3.22) * mm, "endDerivative": vector(-1.52, -4.3) * mm});
            skFitSpline(sketch, "E66", {"points": [v(-23.9, 23.76) * mm, v(-23.1, 20.95) * mm, v(-22.55, 18.27) * mm, v(-21.82, 14.92) * mm, v(-21.52, 13.83) * mm], "startDerivative": vector(3.17, -10.56) * mm, "endDerivative": vector(1.58, -5.4) * mm});
            skFitSpline(sketch, "E67", {"points": [v(-24.21, 27.9) * mm, v(-22.51, 22.68) * mm, v(-21.35, 17.97) * mm, v(-20.13, 14.16) * mm, v(-17.45, 9.83) * mm, v(-15.4, 5.36) * mm, v(-14.74, 3.08) * mm], "startDerivative": vector(9.75, -28.06) * mm, "endDerivative": vector(4.31, -17.05) * mm});
            skFitSpline(sketch, "E68", {"points": [v(-15.17, 2.18) * mm, v(-13.58, 2.68) * mm, v(-11.26, 4.27) * mm], "startDerivative": vector(3.55, 0.78) * mm, "endDerivative": vector(4.23, 3.28) * mm});
            skFitSpline(sketch, "E69", {"points": [v(-28.84, 20.95) * mm, v(-29.07, 17.7) * mm], "startDerivative": vector(-0.23, -3.24) * mm, "endDerivative": vector(-0.23, -3.24) * mm});
            skFitSpline(sketch, "E70", {"points": [v(-29.07, 17.7) * mm, v(-28.3, 17.23) * mm, v(-27.54, 17.4) * mm, v(-27.07, 17.7) * mm], "startDerivative": vector(2.03, -1.73) * mm, "endDerivative": vector(1.48, 1.09) * mm});
            skFitSpline(sketch, "E71", {"points": [v(-27.07, 17.7) * mm, v(-26.6, 22.15) * mm], "startDerivative": vector(0.47, 4.45) * mm, "endDerivative": vector(0.47, 4.45) * mm});
            skFitSpline(sketch, "E72", {"points": [v(-16.22, 18.98) * mm, v(-17.35, 20.77) * mm, v(-19.26, 23.16) * mm, v(-20.1, 24.8) * mm, v(-20.3, 25.4) * mm], "startDerivative": vector(-3.58, 6.44) * mm, "endDerivative": vector(-0.99, 3.66) * mm});
            skFitSpline(sketch, "E73", {"points": [v(-27.43, 30.41) * mm, v(-26.76, 30.55) * mm, v(-25.82, 30.16) * mm, v(-25.68, 29.85) * mm, v(-25.71, 29.5) * mm], "startDerivative": vector(2.18, 0.89) * mm, "endDerivative": vector(-0.3, -1.8) * mm});
            skFitSpline(sketch, "E74", {"points": [v(-9.71, -43.19) * mm, v(-11.44, -48.86) * mm, v(-11.98, -50.81) * mm], "startDerivative": vector(-3.13, -10.16) * mm, "endDerivative": vector(-1.25, -4.6) * mm});
            skSolve(sketch);
        }
        {
            var Q0;
            Q0 = qSketchRegion(id + "F8", true);
            var Q1;
            Q1=sQuery(id+"F8.wireOp",EDGE,"E69");
            var Q2;
            Q2=sQuery(id+"F8.wireOp",EDGE,"E70");
            var Q3;
            Q3=sQuery(id+"F8.wireOp",EDGE,"E71");
            var Q4;
            Q4=sQuery(id+"F8.wireOp",EDGE,"E66");
            var Q5;
            Q5=sQuery(id+"F8.wireOp",EDGE,"E67");
            var Q6;
            Q6=sQuery(id+"F8.wireOp",EDGE,"E68");
            var Q7;
            Q7=sQuery(id+"F8.wireOp",EDGE,"E62");
            var Q8;
            Q8=sQuery(id+"F8.wireOp",EDGE,"E63");
            var Q9;
            Q9=sQuery(id+"F8.wireOp",EDGE,"E64");
            var Q10;
            Q10=sQuery(id+"F8.wireOp",EDGE,"E65");
            var Q11;
            Q11=sQuery(id+"F8.wireOp",EDGE,"E61");
            var Q12;
            Q12=sQuery(id+"F8.wireOp",EDGE,"E60");
            var Q13;
            Q13=sQuery(id+"F8.wireOp",EDGE,"E72");
            var Q14;
            Q14=sQuery(id+"F8.wireOp",EDGE,"E73");
            var Q15;
            Q15=sQuery(id+"F8.wireOp",EDGE,"E74");
            var Q16;
            Q16=sQuery(id+"F8.wireOp",EDGE,"f72cf723-6445-408a-86d6-f7a52dfc5436");
            var Q17;
            Q17=sQuery(id+"F8.wireOp",EDGE,"3cbbcdd0-848f-4456-b324-8c4e4a49c4b9");
            extrude(context, id + "F9", {"entities" : qUnion([Q0]), "bodyType" : ToolBodyType.SURFACE, "surfaceEntities" : qUnion([Q1, Q2, Q3, Q4, Q5, Q6, Q7, Q8, Q9, Q10, Q11, Q12, Q13, Q14, Q15, Q16, Q17]), "depth" : 0.25 * mm});
        }
    });
